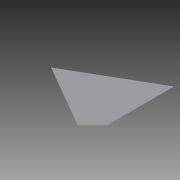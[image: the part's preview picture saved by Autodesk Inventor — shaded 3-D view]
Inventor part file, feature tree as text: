
AUTODESK INVENTOR PART (.ipt)
format: ipt  version: 2015 (Build 190159000, 159)  size: 65,536 bytes
history: native  units: in
note: dims shown in document units (in); Inventor stores cm internally (conversion verified against a paired STEP export)
features: extrude x1, sketch x1
ambient origin geometry x8: Origin, YZ Plane, XZ Plane, XY Plane, X Axis, Y Axis, Z Axis, Center Point
bodies: Solid1 (feature_tree)
feature tree (2):
  extrude  "Extrusion1"  Depth=0.02in TaperAngle=0.0deg
  sketch  "Sketch1"  dims[d2=84.0in d3=0.02in d4=0.0in]
